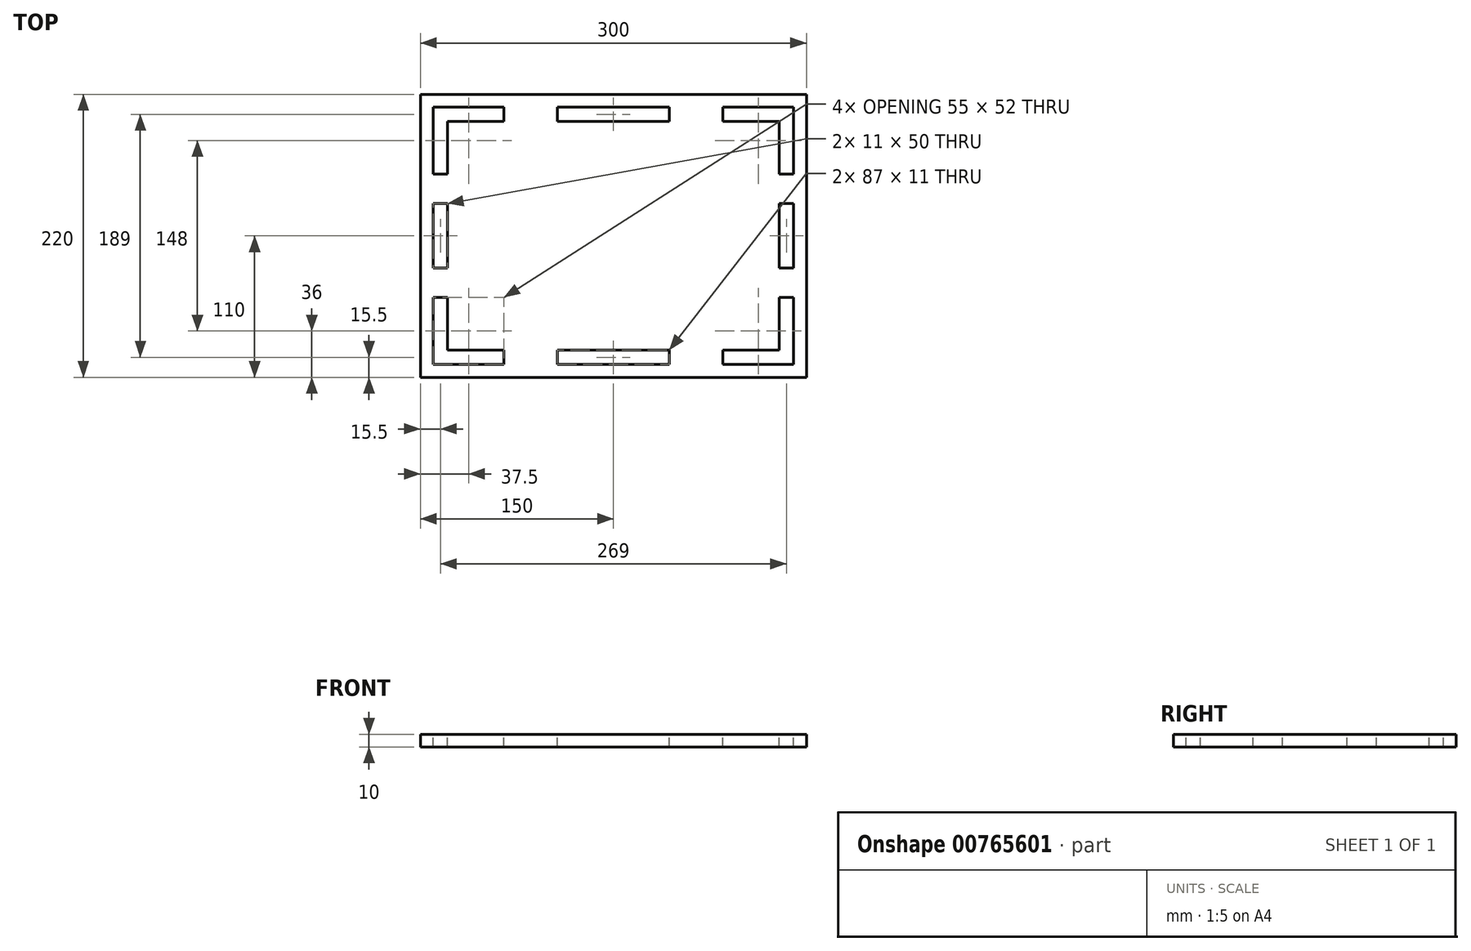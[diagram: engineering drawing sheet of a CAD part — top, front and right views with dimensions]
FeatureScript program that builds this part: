
annotation { "Feature Type Name" : "Feature", "Feature Type Description" : "" }
export const myFeature = defineFeature(function(context is Context, id is Id, definition is map)
    precondition{}
    {
        {
            var Q0;
            Q0=qCreatedBy(makeId("Top.planeOp"),FACE);
            var sketch = newSketch(context, id + "F0", { "sketchPlane" : qUnion([Q0])});
            skLineSegment(sketch, "E0.bottom", {"start": v(-150, 110) * mm, "end": v(150, 110) * mm});
            skLineSegment(sketch, "E0.top", {"start": v(-150, -110) * mm, "end": v(150, -110) * mm});
            skLineSegment(sketch, "E0.left", {"start": v(-150, 110) * mm, "end": v(-150, -110) * mm});
            skLineSegment(sketch, "E0.right", {"start": v(150, 110) * mm, "end": v(150, -110) * mm});
            skLineSegment(sketch, "E1", {"start": v(150, -110) * mm, "end": v(-69, -110) * mm});
            skSolve(sketch);
        }
        {
            var Q0;
            Q0=makeQuery(id+"F0.imprint","IMPRINT",FACE,{"disambiguationData":[TD([[makeQuery(id+"F0.imprint","IMPRINT",EDGE,{"derivedFrom":sQuery(id+"F0.wireOp",EDGE,"E0.bottom")}),-1.0]])]});
            extrude(context, id + "F1", {"entities" : qUnion([Q0]), "depth" : 10 * mm, "offsetDistance" : 25 * mm});
        }
        {
            var Q0;
            Q0=makeQuery(id+"F1.opExtrude","CAP_FACE",FACE,{"disambiguationData":[OSD([sQuery(id+"F0.wireOp",EDGE,"E0.bottom"),sQuery(id+"F0.wireOp",EDGE,"E0.top"),sQuery(id+"F0.wireOp",EDGE,"E0.left"),sQuery(id+"F0.wireOp",EDGE,"E0.right"),sQuery(id+"F0.wireOp",EDGE,"E1"),sQuery(id+"F0.wireOp",EDGE,"hIqJdEga-YKch-AxuA-Qq5S-ZSICDtRFLAnf"),sQuery(id+"F0.wireOp",EDGE,"BsWvy8tO-YPKy-ZXbA-B72n-55CE4LOafWET"),sQuery(id+"F0.wireOp",EDGE,"eAk2glP0-Hkcv-C82K-MrJF-daOROicz4dA9"),sQuery(id+"F0.wireOp",EDGE,"IVzloSqZ-eL4Q-SWWb-zd3C-zllPBfMIFzh1"),sQuery(id+"F0.wireOp",EDGE,"vyz7S1Um-86vA-m5Nb-uxOT-OzOpS84Ckkga"),sQuery(id+"F0.wireOp",EDGE,"K9cV9qPT-6gWa-T3H1-FTnk-ZoYJ1GblVDU5"),sQuery(id+"F0.wireOp",EDGE,"Q96u3hrH-cbIr-Z5xd-YKut-o6HwZpRfjZVX"),sQuery(id+"F0.wireOp",EDGE,"ZKgkDMhc-H8Ha-Jdee-yp7R-CnqooPzm2yzj"),sQuery(id+"F0.wireOp",EDGE,"xi5uXVLV-upHQ-9VTT-pt0p-9DJXMjkZOWVa")])],"isStart":false});
            var sketch = newSketch(context, id + "F2", { "sketchPlane" : qUnion([Q0])});
            skPoint(sketch, "E2.middle", {"position": v(0, 0) * mm});
            skLineSegment(sketch, "E3", {"start": v(140, 100) * mm, "end": v(85, 100) * mm});
            skLineSegment(sketch, "E4", {"start": v(85, 100) * mm, "end": v(85, 89) * mm});
            skLineSegment(sketch, "E5", {"start": v(85, 89) * mm, "end": v(129, 89) * mm});
            skLineSegment(sketch, "E6", {"start": v(140, 100) * mm, "end": v(140, 48) * mm});
            skLineSegment(sketch, "E7", {"start": v(140, 48) * mm, "end": v(129, 48) * mm});
            skLineSegment(sketch, "E8", {"start": v(129, 48) * mm, "end": v(129, 89) * mm});
            skLineSegment(sketch, "E9.MirrorCS", {"start": v(-140, 100) * mm, "end": v(-85, 100) * mm});
            skLineSegment(sketch, "E10.MirrorCS", {"start": v(-85, 100) * mm, "end": v(-85, 89) * mm});
            skLineSegment(sketch, "E11.MirrorCS", {"start": v(-85, 89) * mm, "end": v(-129, 89) * mm});
            skLineSegment(sketch, "E12.MirrorCS", {"start": v(-129, 48) * mm, "end": v(-129, 89) * mm});
            skLineSegment(sketch, "E13.MirrorCS", {"start": v(-140, 48) * mm, "end": v(-129, 48) * mm});
            skLineSegment(sketch, "E14.MirrorCS", {"start": v(-140, 100) * mm, "end": v(-140, 48) * mm});
            skLineSegment(sketch, "E15.MirrorCS", {"start": v(-140, -100) * mm, "end": v(-85, -100) * mm});
            skLineSegment(sketch, "E16.MirrorCS", {"start": v(-140, -100) * mm, "end": v(-140, -48) * mm});
            skLineSegment(sketch, "E17.MirrorCS", {"start": v(-140, -48) * mm, "end": v(-129, -48) * mm});
            skLineSegment(sketch, "E18.MirrorCS", {"start": v(-129, -48) * mm, "end": v(-129, -89) * mm});
            skLineSegment(sketch, "E19.MirrorCS", {"start": v(-85, -89) * mm, "end": v(-129, -89) * mm});
            skLineSegment(sketch, "E20.MirrorCS", {"start": v(-85, -100) * mm, "end": v(-85, -89) * mm});
            skLineSegment(sketch, "E21.MirrorCS", {"start": v(140, -100) * mm, "end": v(85, -100) * mm});
            skLineSegment(sketch, "E22.MirrorCS", {"start": v(85, -100) * mm, "end": v(85, -89) * mm});
            skLineSegment(sketch, "E23.MirrorCS", {"start": v(85, -89) * mm, "end": v(129, -89) * mm});
            skLineSegment(sketch, "E24.MirrorCS", {"start": v(129, -48) * mm, "end": v(129, -89) * mm});
            skLineSegment(sketch, "E25.MirrorCS", {"start": v(140, -48) * mm, "end": v(129, -48) * mm});
            skLineSegment(sketch, "E26.MirrorCS", {"start": v(140, -100) * mm, "end": v(140, -48) * mm});
            skSolve(sketch);
        }
        {
            var Q0;
            Q0=makeQuery(id+"F2.imprint","IMPRINT",FACE,{"disambiguationData":[TD([[makeQuery(id+"F2.imprint","IMPRINT",EDGE,{"derivedFrom":sQuery(id+"F2.wireOp",EDGE,"E3")}),1.0]])]});
            var Q1;
            Q1=makeQuery(id+"F2.imprint","IMPRINT",FACE,{"disambiguationData":[TD([[makeQuery(id+"F2.imprint","IMPRINT",EDGE,{"derivedFrom":sQuery(id+"F2.wireOp",EDGE,"E9.MirrorCS")}),-1.0]])]});
            var Q2;
            Q2=makeQuery(id+"F2.imprint","IMPRINT",FACE,{"disambiguationData":[TD([[makeQuery(id+"F2.imprint","IMPRINT",EDGE,{"derivedFrom":sQuery(id+"F2.wireOp",EDGE,"E16.MirrorCS")}),-1.0]])]});
            var Q3;
            Q3=makeQuery(id+"F2.imprint","IMPRINT",FACE,{"disambiguationData":[TD([[makeQuery(id+"F2.imprint","IMPRINT",EDGE,{"derivedFrom":sQuery(id+"F2.wireOp",EDGE,"E21.MirrorCS")}),-1.0]])]});
            extrude(context, id + "F3", {"entities" : qUnion([Q0, Q1, Q2, Q3]), "operationType" : NewBodyOperationType.REMOVE, "oppositeDirection" : true, "depth" : 10 * mm, "offsetDistance" : 25 * mm});
        }
        {
            var Q0;
            Q0=makeQuery(id+"F1.opExtrude","CAP_FACE",FACE,{"disambiguationData":[OSD([sQuery(id+"F0.wireOp",EDGE,"E0.bottom"),sQuery(id+"F0.wireOp",EDGE,"E0.top"),sQuery(id+"F0.wireOp",EDGE,"E0.left"),sQuery(id+"F0.wireOp",EDGE,"E0.right"),sQuery(id+"F0.wireOp",EDGE,"E1"),sQuery(id+"F0.wireOp",EDGE,"hIqJdEga-YKch-AxuA-Qq5S-ZSICDtRFLAnf"),sQuery(id+"F0.wireOp",EDGE,"BsWvy8tO-YPKy-ZXbA-B72n-55CE4LOafWET"),sQuery(id+"F0.wireOp",EDGE,"eAk2glP0-Hkcv-C82K-MrJF-daOROicz4dA9"),sQuery(id+"F0.wireOp",EDGE,"IVzloSqZ-eL4Q-SWWb-zd3C-zllPBfMIFzh1"),sQuery(id+"F0.wireOp",EDGE,"vyz7S1Um-86vA-m5Nb-uxOT-OzOpS84Ckkga"),sQuery(id+"F0.wireOp",EDGE,"K9cV9qPT-6gWa-T3H1-FTnk-ZoYJ1GblVDU5"),sQuery(id+"F0.wireOp",EDGE,"Q96u3hrH-cbIr-Z5xd-YKut-o6HwZpRfjZVX"),sQuery(id+"F0.wireOp",EDGE,"ZKgkDMhc-H8Ha-Jdee-yp7R-CnqooPzm2yzj"),sQuery(id+"F0.wireOp",EDGE,"xi5uXVLV-upHQ-9VTT-pt0p-9DJXMjkZOWVa")])],"isStart":false});
            var sketch = newSketch(context, id + "F4", { "sketchPlane" : qUnion([Q0])});
            skLineSegment(sketch, "E27", {"start": v(-43.5, -100) * mm, "end": v(-43.5, -89) * mm});
            skLineSegment(sketch, "E28", {"start": v(-43.5, -89) * mm, "end": v(43.5, -89) * mm});
            skLineSegment(sketch, "E29", {"start": v(43.5, -89) * mm, "end": v(43.5, -100) * mm});
            skLineSegment(sketch, "E30", {"start": v(-43.5, -100) * mm, "end": v(43.5, -100) * mm});
            skLineSegment(sketch, "E31.MirrorCS", {"start": v(-43.5, 89) * mm, "end": v(43.5, 89) * mm});
            skLineSegment(sketch, "E32.MirrorCS", {"start": v(-43.5, 100) * mm, "end": v(-43.5, 89) * mm});
            skLineSegment(sketch, "E33.MirrorCS", {"start": v(-43.5, 100) * mm, "end": v(43.5, 100) * mm});
            skLineSegment(sketch, "E34.MirrorCS", {"start": v(43.5, 89) * mm, "end": v(43.5, 100) * mm});
            skSolve(sketch);
        }
        {
            var Q0;
            Q0=makeQuery(id+"F4.imprint","IMPRINT",FACE,{"disambiguationData":[TD([[makeQuery(id+"F4.imprint","IMPRINT",EDGE,{"derivedFrom":sQuery(id+"F4.wireOp",EDGE,"E31.MirrorCS")}),1.0]])]});
            var Q1;
            Q1=makeQuery(id+"F4.imprint","IMPRINT",FACE,{"disambiguationData":[TD([[makeQuery(id+"F4.imprint","IMPRINT",EDGE,{"derivedFrom":sQuery(id+"F4.wireOp",EDGE,"E27")}),-1.0]])]});
            extrude(context, id + "F5", {"entities" : qUnion([Q0, Q1]), "operationType" : NewBodyOperationType.REMOVE, "oppositeDirection" : true, "depth" : 10 * mm, "offsetDistance" : 25 * mm});
        }
        {
            var Q0;
            Q0=makeQuery(id+"F1.opExtrude","CAP_FACE",FACE,{"disambiguationData":[OSD([sQuery(id+"F0.wireOp",EDGE,"E0.bottom"),sQuery(id+"F0.wireOp",EDGE,"E0.top"),sQuery(id+"F0.wireOp",EDGE,"E0.left"),sQuery(id+"F0.wireOp",EDGE,"E0.right"),sQuery(id+"F0.wireOp",EDGE,"E1"),sQuery(id+"F0.wireOp",EDGE,"hIqJdEga-YKch-AxuA-Qq5S-ZSICDtRFLAnf"),sQuery(id+"F0.wireOp",EDGE,"BsWvy8tO-YPKy-ZXbA-B72n-55CE4LOafWET"),sQuery(id+"F0.wireOp",EDGE,"eAk2glP0-Hkcv-C82K-MrJF-daOROicz4dA9"),sQuery(id+"F0.wireOp",EDGE,"IVzloSqZ-eL4Q-SWWb-zd3C-zllPBfMIFzh1"),sQuery(id+"F0.wireOp",EDGE,"vyz7S1Um-86vA-m5Nb-uxOT-OzOpS84Ckkga"),sQuery(id+"F0.wireOp",EDGE,"K9cV9qPT-6gWa-T3H1-FTnk-ZoYJ1GblVDU5"),sQuery(id+"F0.wireOp",EDGE,"Q96u3hrH-cbIr-Z5xd-YKut-o6HwZpRfjZVX"),sQuery(id+"F0.wireOp",EDGE,"ZKgkDMhc-H8Ha-Jdee-yp7R-CnqooPzm2yzj"),sQuery(id+"F0.wireOp",EDGE,"xi5uXVLV-upHQ-9VTT-pt0p-9DJXMjkZOWVa")])],"isStart":false});
            var sketch = newSketch(context, id + "F6", { "sketchPlane" : qUnion([Q0])});
            skLineSegment(sketch, "E35", {"start": v(140, 0) * mm, "end": v(140, -25) * mm});
            skLineSegment(sketch, "E36", {"start": v(140, -25) * mm, "end": v(140, 25) * mm});
            skLineSegment(sketch, "E37", {"start": v(140, -25) * mm, "end": v(129, -25) * mm});
            skLineSegment(sketch, "E38", {"start": v(129, 25) * mm, "end": v(140, 25) * mm});
            skLineSegment(sketch, "E39", {"start": v(129, -25) * mm, "end": v(129, 25) * mm});
            skLineSegment(sketch, "E40.MirrorCS", {"start": v(-129, -25) * mm, "end": v(-129, 25) * mm});
            skLineSegment(sketch, "E41.MirrorCS", {"start": v(-140, -25) * mm, "end": v(-129, -25) * mm});
            skLineSegment(sketch, "E42.MirrorCS", {"start": v(-140, -25) * mm, "end": v(-140, 25) * mm});
            skLineSegment(sketch, "E43.MirrorCS", {"start": v(-129, 25) * mm, "end": v(-140, 25) * mm});
            skSolve(sketch);
        }
        {
            var Q0;
            Q0=makeQuery(id+"F6.imprint","IMPRINT",FACE,{"disambiguationData":[TD([[makeQuery(id+"F6.imprint","IMPRINT",EDGE,{"derivedFrom":sQuery(id+"F6.wireOp",EDGE,"E40.MirrorCS")}),1.0]])]});
            var Q1;
            {var subQ1=sQuery(id+"F6.wireOp",EDGE,"E37");Q1=makeQuery(id+"F6.imprint","IMPRINT",FACE,{"disambiguationData":[TD([[makeQuery(id+"F6.imprint","IMPRINT",EDGE,{"derivedFrom":subQ1}),-1.0]])]});}
            extrude(context, id + "F7", {"entities" : qUnion([Q0, Q1]), "operationType" : NewBodyOperationType.REMOVE, "oppositeDirection" : true, "depth" : 10 * mm, "offsetDistance" : 25 * mm});
        }
    });
